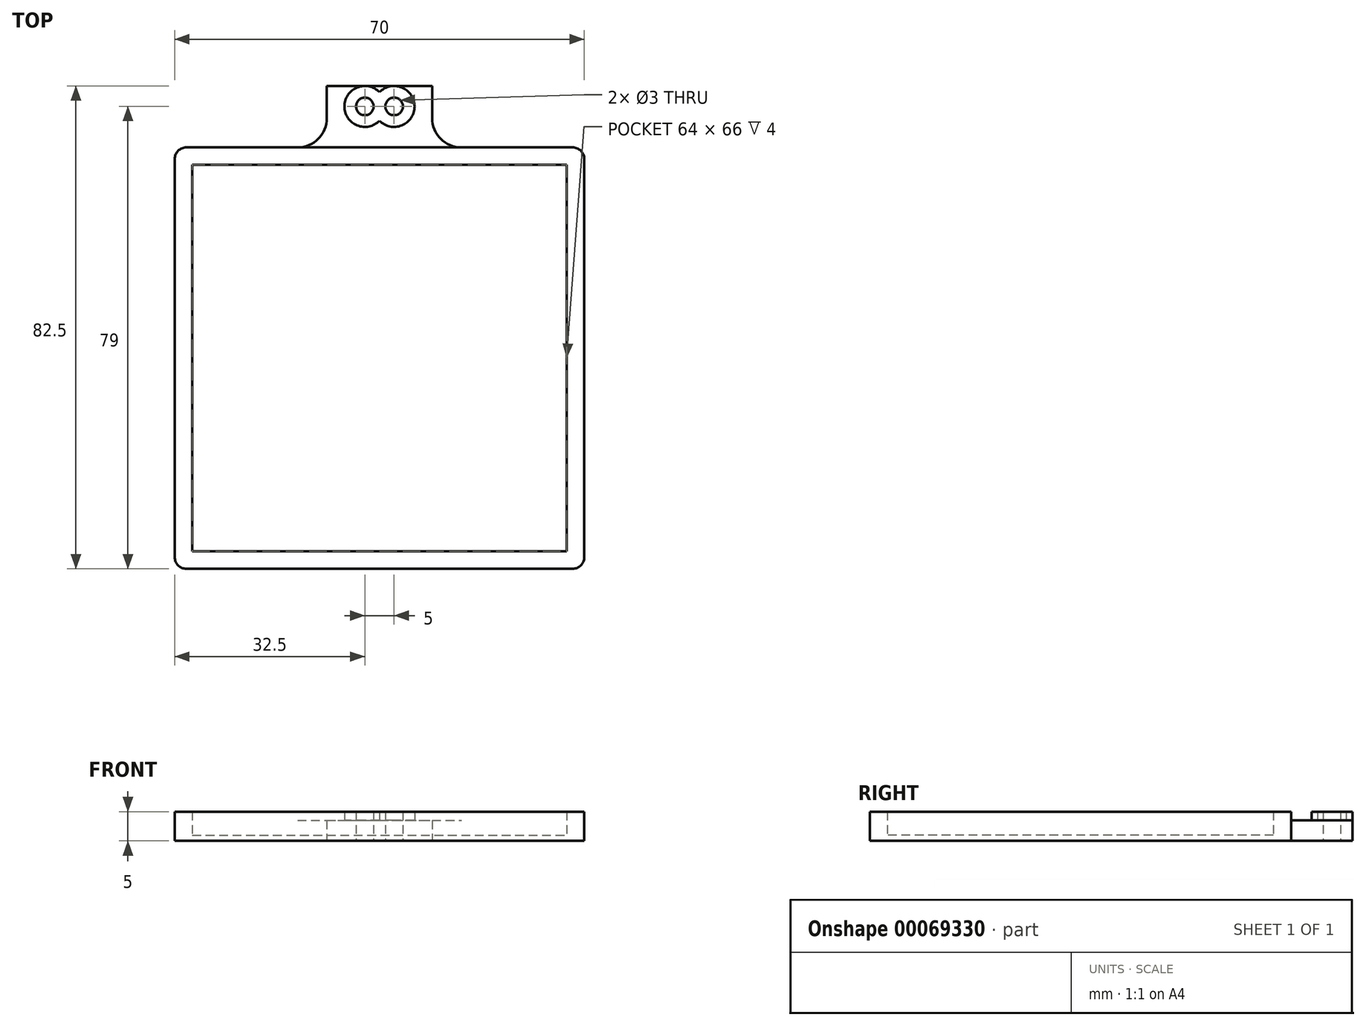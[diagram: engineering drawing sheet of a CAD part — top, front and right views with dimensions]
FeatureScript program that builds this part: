
annotation { "Feature Type Name" : "Feature", "Feature Type Description" : "" }
export const myFeature = defineFeature(function(context is Context, id is Id, definition is map)
    precondition{}
    {
        {
            var Q0;
            Q0=qCreatedBy(makeId("Top.planeOp"),FACE);
            var sketch = newSketch(context, id + "F0", { "sketchPlane" : qUnion([Q0])});
            skLineSegment(sketch, "E0", {"start": v(0, 64.66) * mm, "end": v(0, -69.28) * mm, "construction": true});
            skLineSegment(sketch, "E1.0", {"start": v(-35, 64.66) * mm, "end": v(-35, -69.28) * mm, "construction": true});
            skLineSegment(sketch, "E2.0", {"start": v(35, 64.66) * mm, "end": v(35, -69.28) * mm, "construction": true});
            skLineSegment(sketch, "E3", {"start": v(-56.35, 0) * mm, "end": v(65.82, 0) * mm, "construction": true});
            skLineSegment(sketch, "E4.0", {"start": v(-56.35, -36) * mm, "end": v(65.82, -36) * mm, "construction": true});
            skLineSegment(sketch, "E5.0", {"start": v(-56.35, 36) * mm, "end": v(-14, 36) * mm, "construction": true});
            skLineSegment(sketch, "E6.0", {"start": v(-56.35, 33) * mm, "end": v(65.82, 33) * mm, "construction": true});
            skLineSegment(sketch, "E7.0", {"start": v(-56.35, -33) * mm, "end": v(32, -33) * mm, "construction": true});
            skLineSegment(sketch, "E8.0", {"start": v(-32, 64.66) * mm, "end": v(-32, 33) * mm, "construction": true});
            skLineSegment(sketch, "E9.0", {"start": v(32, 64.66) * mm, "end": v(32, 33) * mm, "construction": true});
            skLineSegment(sketch, "E10", {"start": v(14, 36) * mm, "end": v(35, 36) * mm});
            skLineSegment(sketch, "E11", {"start": v(35, 36) * mm, "end": v(35, -36) * mm});
            skLineSegment(sketch, "E12", {"start": v(35, -36) * mm, "end": v(-35, -36) * mm});
            skLineSegment(sketch, "E13", {"start": v(-35, -36) * mm, "end": v(-35, 36) * mm});
            skLineSegment(sketch, "E14", {"start": v(-32, 33) * mm, "end": v(32, 33) * mm});
            skLineSegment(sketch, "E15", {"start": v(35, 33) * mm, "end": v(35, -33) * mm});
            skLineSegment(sketch, "E16", {"start": v(32, -33) * mm, "end": v(-32, -33) * mm});
            skLineSegment(sketch, "E17.0", {"start": v(-56.35, 14.5) * mm, "end": v(-22, 14.5) * mm, "construction": true});
            skLineSegment(sketch, "E18.trimOffspring", {"start": v(12, -2) * mm, "end": v(35, -2) * mm, "construction": true});
            skLineSegment(sketch, "E19.0", {"start": v(-22, 64.66) * mm, "end": v(-22, 36) * mm, "construction": true});
            skLineSegment(sketch, "E20.trimOffspring", {"start": v(-32, 14.5) * mm, "end": v(-32, -14) * mm, "construction": true});
            skLineSegment(sketch, "E21.trimOffspring", {"start": v(-22, 33) * mm, "end": v(-22, 14.5) * mm, "construction": true});
            skLineSegment(sketch, "E22", {"start": v(-32, 14.5) * mm, "end": v(-22, 14.5) * mm});
            skLineSegment(sketch, "E23.0", {"start": v(12, 64.66) * mm, "end": v(12, 36) * mm, "construction": true});
            skLineSegment(sketch, "E24.trimOffspring", {"start": v(12, 33) * mm, "end": v(12, -2) * mm, "construction": true});
            skLineSegment(sketch, "E25.trimOffspring", {"start": v(32, 0) * mm, "end": v(32, -33) * mm, "construction": true});
            skLineSegment(sketch, "E26", {"start": v(12, 0) * mm, "end": v(12, -2) * mm});
            skLineSegment(sketch, "E27", {"start": v(32, -2) * mm, "end": v(12, -2) * mm});
            skLineSegment(sketch, "E28.0", {"start": v(-56.35, -14) * mm, "end": v(-8, -14) * mm, "construction": true});
            skLineSegment(sketch, "E29.trimOffspring", {"start": v(-8, -14) * mm, "end": v(-8, -33) * mm, "construction": true});
            skLineSegment(sketch, "E30.trimOffspring", {"start": v(-8, -36) * mm, "end": v(-8, -74.28) * mm, "construction": true});
            skLineSegment(sketch, "E31.trimOffspring", {"start": v(-32, -36) * mm, "end": v(-32, -69.28) * mm, "construction": true});
            skLineSegment(sketch, "E32", {"start": v(-8, -33) * mm, "end": v(-8, -14) * mm});
            skLineSegment(sketch, "E33.0", {"start": v(24.75, 64.66) * mm, "end": v(24.75, 33) * mm, "construction": true});
            skLineSegment(sketch, "E34.trimOffspring", {"start": v(24.75, 0) * mm, "end": v(24.75, -69.28) * mm, "construction": true});
            skLineSegment(sketch, "E35.0", {"start": v(-56.35, -22.75) * mm, "end": v(0, -22.75) * mm, "construction": true});
            skLineSegment(sketch, "E36.trimOffspring", {"start": v(24.75, -22.75) * mm, "end": v(65.82, -22.75) * mm, "construction": true});
            skLineSegment(sketch, "E37", {"start": v(24.75, -12.5) * mm, "end": v(32, -12.5) * mm});
            skLineSegment(sketch, "E38.0", {"start": v(-32, 10.5) * mm, "end": v(-17, 10.5) * mm});
            skLineSegment(sketch, "E39.0", {"start": v(-18, 26) * mm, "end": v(-18, 7.5) * mm});
            skLineSegment(sketch, "E40.0", {"start": v(8, 26) * mm, "end": v(8, -2) * mm});
            skLineSegment(sketch, "E41", {"start": v(17.71, -12.5) * mm, "end": v(8, -12.5) * mm});
            skLineSegment(sketch, "E42", {"start": v(8, -2) * mm, "end": v(8, -12.5) * mm});
            skLineSegment(sketch, "E43", {"start": v(-18, 10.5) * mm, "end": v(-18, 7.5) * mm});
            skLineSegment(sketch, "E44", {"start": v(-17, 10.5) * mm, "end": v(-18, 10.5) * mm});
            skLineSegment(sketch, "E45.0", {"start": v(-4, -31) * mm, "end": v(-4, -12) * mm});
            skLineSegment(sketch, "E46", {"start": v(-8, -10) * mm, "end": v(-4, -10) * mm});
            skLineSegment(sketch, "E47", {"start": v(-4, -10) * mm, "end": v(-4, -12) * mm});
            skArc(sketch, "E48", {"start": v(17.71, -12.5) * mm, "mid": v(8.46, -21.1) * mm, "end": v(12.71, -33) * mm});
            skLineSegment(sketch, "E49", {"start": v(32, -2) * mm, "end": v(32, -12.5) * mm});
            skLineSegment(sketch, "E50", {"start": v(-32, 14.5) * mm, "end": v(-32, 10.5) * mm});
            skLineSegment(sketch, "E51", {"start": v(-32, 10.5) * mm, "end": v(-32, -14) * mm});
            skPoint(sketch, "E52.orphan", {"position": v(35, -12.5) * mm});
            skLineSegment(sketch, "E53.trimOffspring", {"start": v(32, -36) * mm, "end": v(32, -69.28) * mm, "construction": true});
            skLineSegment(sketch, "E54.trimOffspring", {"start": v(35, -33) * mm, "end": v(65.82, -33) * mm, "construction": true});
            skLineSegment(sketch, "E55", {"start": v(-32, -14) * mm, "end": v(-32, -33) * mm});
            skLineSegment(sketch, "E56", {"start": v(32, -12.5) * mm, "end": v(32, -33) * mm});
            skLineSegment(sketch, "E57", {"start": v(32, 33) * mm, "end": v(32, -2) * mm});
            skLineSegment(sketch, "E58", {"start": v(-32, 33) * mm, "end": v(-32, 14.5) * mm});
            skLineSegment(sketch, "E59.0", {"start": v(-56.35, 46.5) * mm, "end": v(65.82, 46.5) * mm, "construction": true});
            skLineSegment(sketch, "E60", {"start": v(0, 46.5) * mm, "end": v(0, 36) * mm, "construction": true});
            skLineSegment(sketch, "E61.0", {"start": v(-9, 46.5) * mm, "end": v(-9, 41) * mm});
            skLineSegment(sketch, "E62.0", {"start": v(9, 46.5) * mm, "end": v(9, 41) * mm});
            skLineSegment(sketch, "E63", {"start": v(-9, 46.5) * mm, "end": v(9, 46.5) * mm});
            skLineSegment(sketch, "E64.0", {"start": v(-9, 43) * mm, "end": v(9, 43) * mm, "construction": true});
            skLineSegment(sketch, "E65.0", {"start": v(-2.5, 46.5) * mm, "end": v(-2.5, 36) * mm, "construction": true});
            skCircle(sketch, "E66", {"center": v(-2.5, 43) * mm, "radius": 1.5 * mm});
            skArc(sketch, "E67", {"start": v(0, 45.45) * mm, "mid": v(-6, 43) * mm, "end": v(0, 40.55) * mm});
            skArc(sketch, "E68.MirrorC", {"start": v(0, 45.45) * mm, "mid": v(6, 43) * mm, "end": v(0, 40.55) * mm});
            skCircle(sketch, "E69.MirrorC", {"center": v(2.5, 43) * mm, "radius": 1.5 * mm});
            skPoint(sketch, "E70.newPointB", {"position": v(-35, 36) * mm});
            skArc(sketch, "E70.filletArc", {"start": v(9, 41) * mm, "mid": v(10.46, 37.46) * mm, "end": v(14, 36) * mm});
            skArc(sketch, "E71.filletArc", {"start": v(-14, 36) * mm, "mid": v(-10.46, 37.46) * mm, "end": v(-9, 41) * mm});
            skLineSegment(sketch, "E72", {"start": v(-14, 36) * mm, "end": v(-35, 36) * mm});
            skLineSegment(sketch, "E73", {"start": v(-14, 36) * mm, "end": v(14, 36) * mm});
            skSolve(sketch);
        }
        {
            var Q0;
            {var subQ0=sQuery(id+"F0.wireOp",EDGE,"E50");Q0=makeQuery(id+"F0.imprint","IMPRINT",FACE,{"disambiguationData":[TD([[makeQuery(id+"F0.imprint","IMPRINT",EDGE,{"derivedFrom":subQ0}),-1.0]])]});}
            var Q1;
            {var subQ1=sQuery(id+"F0.wireOp",EDGE,"E12");Q1=makeQuery(id+"F0.imprint","IMPRINT",FACE,{"disambiguationData":[TD([[makeQuery(id+"F0.imprint","IMPRINT",EDGE,{"derivedFrom":subQ1}),-1.0]])]});}
            var Q2;
            {var subQ4=sQuery(id+"F0.wireOp",EDGE,"E10");Q2=makeQuery(id+"F0.imprint","IMPRINT",FACE,{"disambiguationData":[TD([[makeQuery(id+"F0.imprint","IMPRINT",EDGE,{"derivedFrom":subQ4}),-1.0]])]});}
            var Q3;
            {var subQ5=sQuery(id+"F0.wireOp",EDGE,"E49");Q3=makeQuery(id+"F0.imprint","IMPRINT",FACE,{"disambiguationData":[TD([[makeQuery(id+"F0.imprint","IMPRINT",EDGE,{"derivedFrom":subQ5}),1.0]])]});}
            var Q4;
            Q4=makeQuery(id+"F0.imprint","IMPRINT",FACE,{"disambiguationData":[TD([[makeQuery(id+"F0.imprint","IMPRINT",EDGE,{"derivedFrom":sQuery(id+"F0.wireOp",EDGE,"E66")}),-1.0]])]});
            extrude(context, id + "F1", {"entities" : qUnion([Q0, Q1, Q2, Q3, Q4]), "depth" : 5 * mm});
        }
        {
            var Q0;
            {var subQ4=sQuery(id+"F0.wireOp",EDGE,"E61.0");Q0=makeQuery(id+"F0.imprint","IMPRINT",FACE,{"disambiguationData":[TD([[makeQuery(id+"F0.imprint","IMPRINT",EDGE,{"derivedFrom":subQ4}),1.0]])]});}
            var Q1;
            {var subQ0=sQuery(id+"F0.wireOp",EDGE,"E67");var subQ1=sQuery(id+"F0.wireOp",EDGE,"E63");var subQ2=makeQuery(id+"F0.imprint","INTERSECT",VERTEX,{"derivedFrom":[subQ1,subQ0]});Q1=makeQuery(id+"F0.imprint","IMPRINT",FACE,{"disambiguationData":[TD([[makeQuery(id+"F0.imprint","IMPRINT",EDGE,{"disambiguationData":[TD([[subQ2,-1.0]])],"derivedFrom":subQ1}),-1.0]])]});}
            extrude(context, id + "F2", {"entities" : qUnion([Q0, Q1]), "operationType" : NewBodyOperationType.ADD, "depth" : 3.5 * mm});
        }
        {
            var Q0;
            {var subQ0=sQuery(id+"F0.wireOp",EDGE,"4MRV2adj-cE5r-6kMD-PRN0-LQWbbjDhki69");Q0=makeQuery(id+"F0.imprint","IMPRINT",FACE,{"disambiguationData":[TD([[makeQuery(id+"F0.imprint","IMPRINT",EDGE,{"derivedFrom":subQ0}),1.0]])]});}
            var Q1;
            {var subQ3=sQuery(id+"F0.wireOp",EDGE,"E26");Q1=makeQuery(id+"F0.imprint","IMPRINT",FACE,{"disambiguationData":[TD([[makeQuery(id+"F0.imprint","IMPRINT",EDGE,{"derivedFrom":subQ3}),-1.0]])]});}
            var Q2;
            {var subQ1=sQuery(id+"F0.wireOp",EDGE,"E32");Q2=makeQuery(id+"F0.imprint","IMPRINT",FACE,{"disambiguationData":[TD([[makeQuery(id+"F0.imprint","IMPRINT",EDGE,{"derivedFrom":subQ1}),-1.0]])]});}
            var Q3;
            Q3=makeQuery(id+"F0.imprint","IMPRINT",FACE,{"disambiguationData":[TD([[makeQuery(id+"F0.imprint","IMPRINT",EDGE,{"derivedFrom":sQuery(id+"F0.wireOp",EDGE,"E14")}),-1.0]])]});
            extrude(context, id + "F3", {"entities" : qUnion([Q0, Q1, Q2, Q3]), "operationType" : NewBodyOperationType.ADD, "depth" : 1 * mm});
        }
        {
            var Q0;
            Q0=makeQuery(id+"F1.opExtrude","SWEPT_EDGE",EDGE,{"disambiguationData":[OSD([sQuery(id+"F0.wireOp",EDGE,"E12"),sQuery(id+"F0.wireOp",EDGE,"E13")])]});
            var Q1;
            Q1=makeQuery(id+"F1.opExtrude","SWEPT_EDGE",EDGE,{"disambiguationData":[OSD([sQuery(id+"F0.wireOp",EDGE,"E11"),sQuery(id+"F0.wireOp",EDGE,"E12")])]});
            var Q2;
            Q2=makeQuery(id+"F1.opExtrude","SWEPT_EDGE",EDGE,{"disambiguationData":[OSD([sQuery(id+"F0.wireOp",EDGE,"E13"),sQuery(id+"F0.wireOp",EDGE,"E72")])]});
            var Q3;
            Q3=makeQuery(id+"F1.opExtrude","SWEPT_EDGE",EDGE,{"disambiguationData":[OSD([sQuery(id+"F0.wireOp",EDGE,"E10"),sQuery(id+"F0.wireOp",EDGE,"E11")])]});
            fillet(context, id + "F4", {"entities" : qUnion([Q0, Q1, Q2, Q3]), "radius" : 2 * mm, "tangentPropagation" : true, "allowEdgeOverflow" : false});
        }
    });
